# Revit family: IS_Contour21_S2639_BIM_BE
name_source: partatom
category: Plumbing Fixtures
revit_build: Autodesk Revit 2015 (Build: 20140606_1530(x64)
units: mm (PartAtom-declared; Revit-internal decimal feet)

## types (1)
- S263901 - Contour 21 Lavabo 40cm 1KG sans trop-plein
    Accesoires = www.idealstandard.be
    Afwerking = Wit
    Auteur = Ideal Standard Produktions-GmbH
    Barcode = 5017830476429
    Beschrijvinggarantie = Fabrieksgarantie
    BimObjectNaam = ISI_IdealStandard_Lavabo_Contour_S263901
    Breedte = 0
    BrutoGewicht = 0
    Cost = 0 $
    Default Elevation = 845 mm
    Description = Contour 21 Lavabo 40cm 1KG sans trop-plein
    Diepte = 0 mm  [stored 0 ft]
    Dimensions = 328 x 401 x 160 mm
    DuurEenheid = jaar
    Eigenschappen = Contour 21 School kinderwastafel 400mm in porselein.
    Garantieonderdelen = 10
    GrootteAfvoergat = 0
    Hauteur = 160 mm
    IfcExportAs = IfcSanitaryTerminalType
    IfcExportType = WASHHANDBASINS
    Installatieinstructies = www.idealstandard.be
    Kleur = Wit
    Largeur = 401 mm
    Lengte = 0 mm  [stored 0 ft]
    Longueur = 328 mm
    Manufacturer = www.idealstandard.be
    Materiaal = porselein
    Merk = Ideal Standard
    Model = S263901
    Nettogewicht = 7.4
    Ophangingwastafel = muurbevestiging
    Productinformatie = www.idealstandard.be
    Telefoonnummer = 0032 2 325 66 00
    Typeconnectie = Sanitair
    Typewastafel = kinderwastafel
    URL = www.idealstandard.be
    Uniclass2015Beschrijving = Wash basins, sinks and troughs
    Uniclass2015Referentie = Pr_40_20_96
    Uniclass2015Version = Products v1.1
    Urlproducent = www.idealstandard.be
    Versie = 1
    Vervangingskosten = 0
    Verwachtelevensduur = 25 jaar
    Volumeunits = liter

note: [stored X ft] marks values corroborated as IEEE doubles in the binary element streams (Revit-internal decimal feet)

## geometry (parser evidence)
native form markers: Blend x4, Sweep x1
no freeform markers — native parametric forms only
